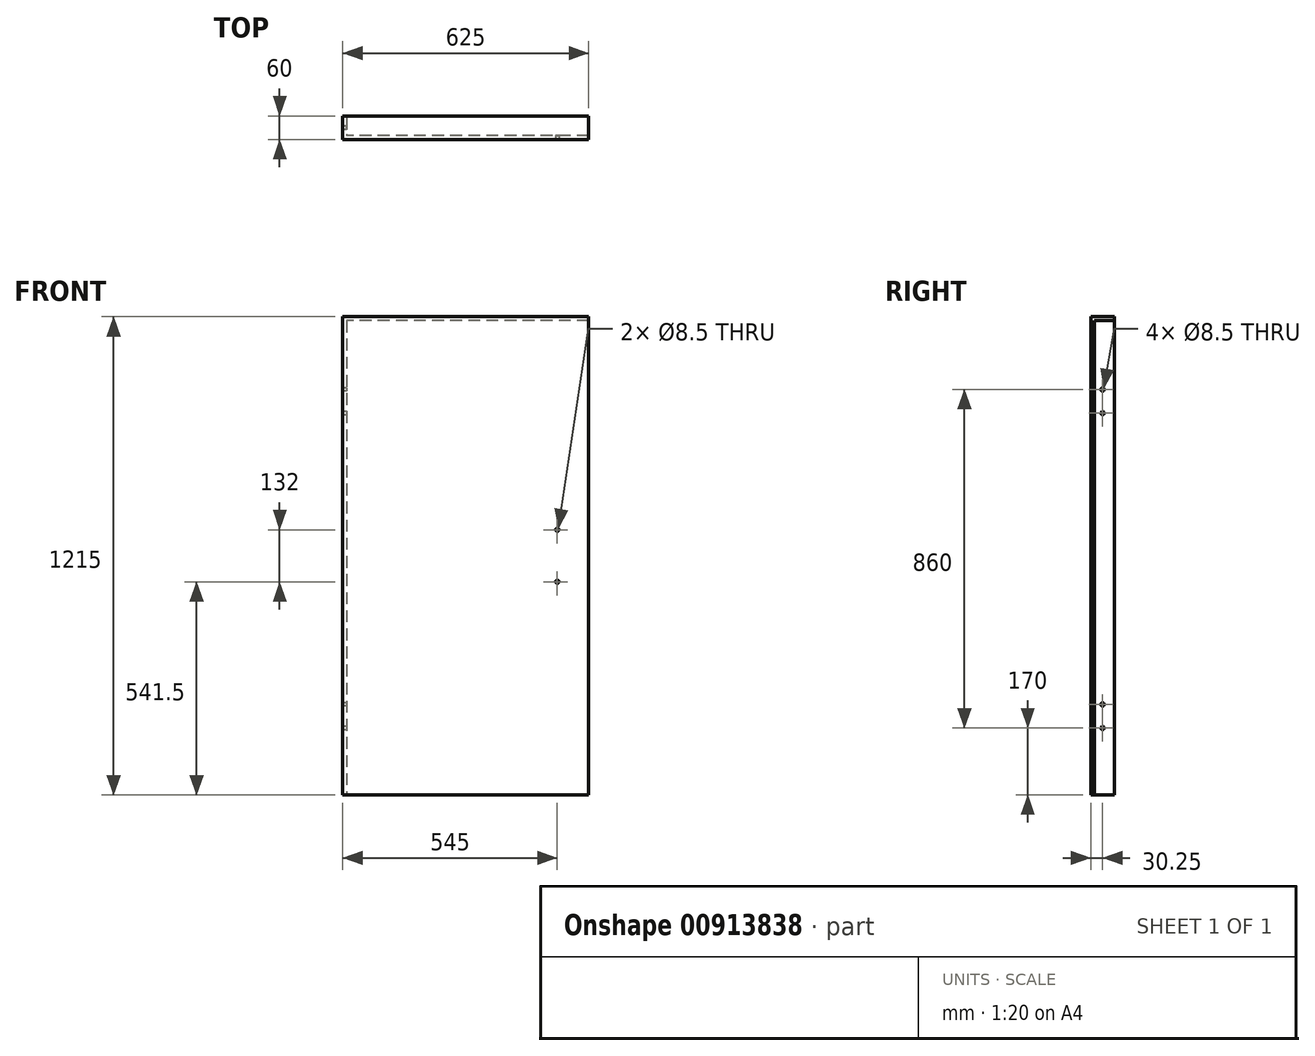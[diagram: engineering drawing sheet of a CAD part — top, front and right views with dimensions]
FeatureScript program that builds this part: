
annotation { "Feature Type Name" : "Feature", "Feature Type Description" : "" }
export const myFeature = defineFeature(function(context is Context, id is Id, definition is map)
    precondition{}
    {
        {
            var Q0;
            Q0=qCreatedBy(makeId("Front.planeOp"),FACE);
            var sketch = newSketch(context, id + "F0", { "sketchPlane" : qUnion([Q0])});
            skLineSegment(sketch, "E0.bottom", {"start": v(312.5, 607.5) * mm, "end": v(-312.5, 607.5) * mm});
            skLineSegment(sketch, "E0.top", {"start": v(312.5, -607.5) * mm, "end": v(-312.5, -607.5) * mm});
            skLineSegment(sketch, "E0.left", {"start": v(312.5, 607.5) * mm, "end": v(312.5, -607.5) * mm});
            skLineSegment(sketch, "E0.right", {"start": v(-312.5, 607.5) * mm, "end": v(-312.5, -607.5) * mm});
            skPoint(sketch, "E0.middle", {"position": v(0, 0) * mm});
            skSolve(sketch);
        }
        {
            var Q0;
            Q0=makeQuery(id+"F0.imprint","IMPRINT",FACE,{"disambiguationData":[TD([[makeQuery(id+"F0.imprint","IMPRINT",EDGE,{"derivedFrom":sQuery(id+"F0.wireOp",EDGE,"E0.bottom")}),1.0]])]});
            extrude(context, id + "F1", {"entities" : qUnion([Q0]), "depth" : 10 * mm, "offsetDistance" : 25 * mm});
        }
        {
            var Q0;
            Q0=makeQuery(id+"F1.opExtrude","CAP_FACE",FACE,{"disambiguationData":[OSD([sQuery(id+"F0.wireOp",EDGE,"E0.bottom"),sQuery(id+"F0.wireOp",EDGE,"E0.top"),sQuery(id+"F0.wireOp",EDGE,"E0.left"),sQuery(id+"F0.wireOp",EDGE,"E0.right")])],"isStart":true});
            var sketch = newSketch(context, id + "F2", { "sketchPlane" : qUnion([Q0])});
            skLineSegment(sketch, "E1.0", {"start": v(-312.5, 607.5) * mm, "end": v(312.5, 607.5) * mm});
            skLineSegment(sketch, "E2.0", {"start": v(312.5, 607.5) * mm, "end": v(312.5, -607.5) * mm});
            skLineSegment(sketch, "E3.0", {"start": v(302.5, 597.5) * mm, "end": v(302.5, -607.5) * mm});
            skLineSegment(sketch, "E3.1", {"start": v(-357.5, 597.5) * mm, "end": v(302.5, 597.5) * mm});
            skSolve(sketch);
        }
        {
            var Q0;
            {var subQ3=sQuery(id+"F2.wireOp",EDGE,"E1.0");Q0=makeQuery(id+"F2.imprint","IMPRINT",FACE,{"disambiguationData":[TD([[makeQuery(id+"F2.imprint","IMPRINT",EDGE,{"derivedFrom":subQ3}),-1.0]])]});}
            extrude(context, id + "F3", {"entities" : qUnion([Q0]), "operationType" : NewBodyOperationType.ADD, "depth" : 50 * mm, "offsetDistance" : 25 * mm});
        }
        {
            var Q0;
            Q0=makeQuery(id+"F1.opExtrude","CAP_FACE",FACE,{"disambiguationData":[OSD([sQuery(id+"F0.wireOp",EDGE,"E0.bottom"),sQuery(id+"F0.wireOp",EDGE,"E0.top"),sQuery(id+"F0.wireOp",EDGE,"E0.left"),sQuery(id+"F0.wireOp",EDGE,"E0.right")])],"isStart":false});
            var sketch = newSketch(context, id + "F4", { "sketchPlane" : qUnion([Q0])});
            skLineSegment(sketch, "E4", {"start": v(0, 0) * mm, "end": v(232.5, 0) * mm});
            skLineSegment(sketch, "E5", {"start": v(232.5, 66) * mm, "end": v(232.5, -66) * mm});
            skPoint(sketch, "E6", {"position": v(232.5, 66) * mm});
            skPoint(sketch, "E7", {"position": v(232.5, -66) * mm});
            skSolve(sketch);
        }
        {
            var Q0;
            Q0=sQuery(id+"F4.wireOp",VERTEX,"E6");
            var Q1;
            Q1=sQuery(id+"F4.wireOp",VERTEX,"E7");
            var Q2;
            Q2=makeQuery(id+"F1.opExtrude","SWEPT_BODY",BODY,{"disambiguationData":[OSD([sQuery(id+"F0.wireOp",EDGE,"E0.bottom"),sQuery(id+"F0.wireOp",EDGE,"E0.top"),sQuery(id+"F0.wireOp",EDGE,"E0.left"),sQuery(id+"F0.wireOp",EDGE,"E0.right")])]});
            hole(context, id + "F5", {"style" : HoleStyle.SIMPLE, "endStyle" : HoleEndStyle.THROUGH, "holeDiameter" : 8.5 * mm, "majorDiameter" : 5 * mm, "isTappedThrough" : true, "tappedDepth" : 12 * mm, "tapClearance" : 3, "locations" : qUnion([Q0, Q1]), "scope" : qUnion([Q2])});
        }
        {
            var Q0;
            Q0=makeQuery(id+"F3.boolean.opBoolean","MERGE",FACE,{"derivedFrom":[makeQuery(id+"F1.opExtrude","SWEPT_FACE",FACE,{"disambiguationData":[OSD([sQuery(id+"F0.wireOp",EDGE,"E0.right")])]}),makeQuery(id+"F3.opExtrude","SWEPT_FACE",FACE,{"disambiguationData":[OSD([sQuery(id+"F2.wireOp",EDGE,"E2.0")])]})]});
            var sketch = newSketch(context, id + "F6", { "sketchPlane" : qUnion([Q0])});
            skPoint(sketch, "E8", {"position": v(-20.25, 422.5) * mm});
            skPoint(sketch, "E9", {"position": v(-20.25, 362.5) * mm});
            skPoint(sketch, "E10", {"position": v(-20.25, -377.5) * mm});
            skPoint(sketch, "E11", {"position": v(-20.25, -437.5) * mm});
            skSolve(sketch);
        }
        {
            var Q0;
            Q0=sQuery(id+"F6.wireOp",VERTEX,"E8");
            var Q1;
            Q1=sQuery(id+"F6.wireOp",VERTEX,"E9");
            var Q2;
            Q2=sQuery(id+"F6.wireOp",VERTEX,"E10");
            var Q3;
            Q3=sQuery(id+"F6.wireOp",VERTEX,"E11");
            var Q4;
            Q4=makeQuery(id+"F1.opExtrude","SWEPT_BODY",BODY,{"disambiguationData":[OSD([sQuery(id+"F0.wireOp",EDGE,"E0.bottom"),sQuery(id+"F0.wireOp",EDGE,"E0.top"),sQuery(id+"F0.wireOp",EDGE,"E0.left"),sQuery(id+"F0.wireOp",EDGE,"E0.right")])]});
            hole(context, id + "F7", {"style" : HoleStyle.SIMPLE, "endStyle" : HoleEndStyle.THROUGH, "holeDiameter" : 8.5 * mm, "majorDiameter" : 5 * mm, "isTappedThrough" : true, "tappedDepth" : 12 * mm, "tapClearance" : 3, "locations" : qUnion([Q0, Q1, Q2, Q3]), "scope" : qUnion([Q4])});
        }
    });
